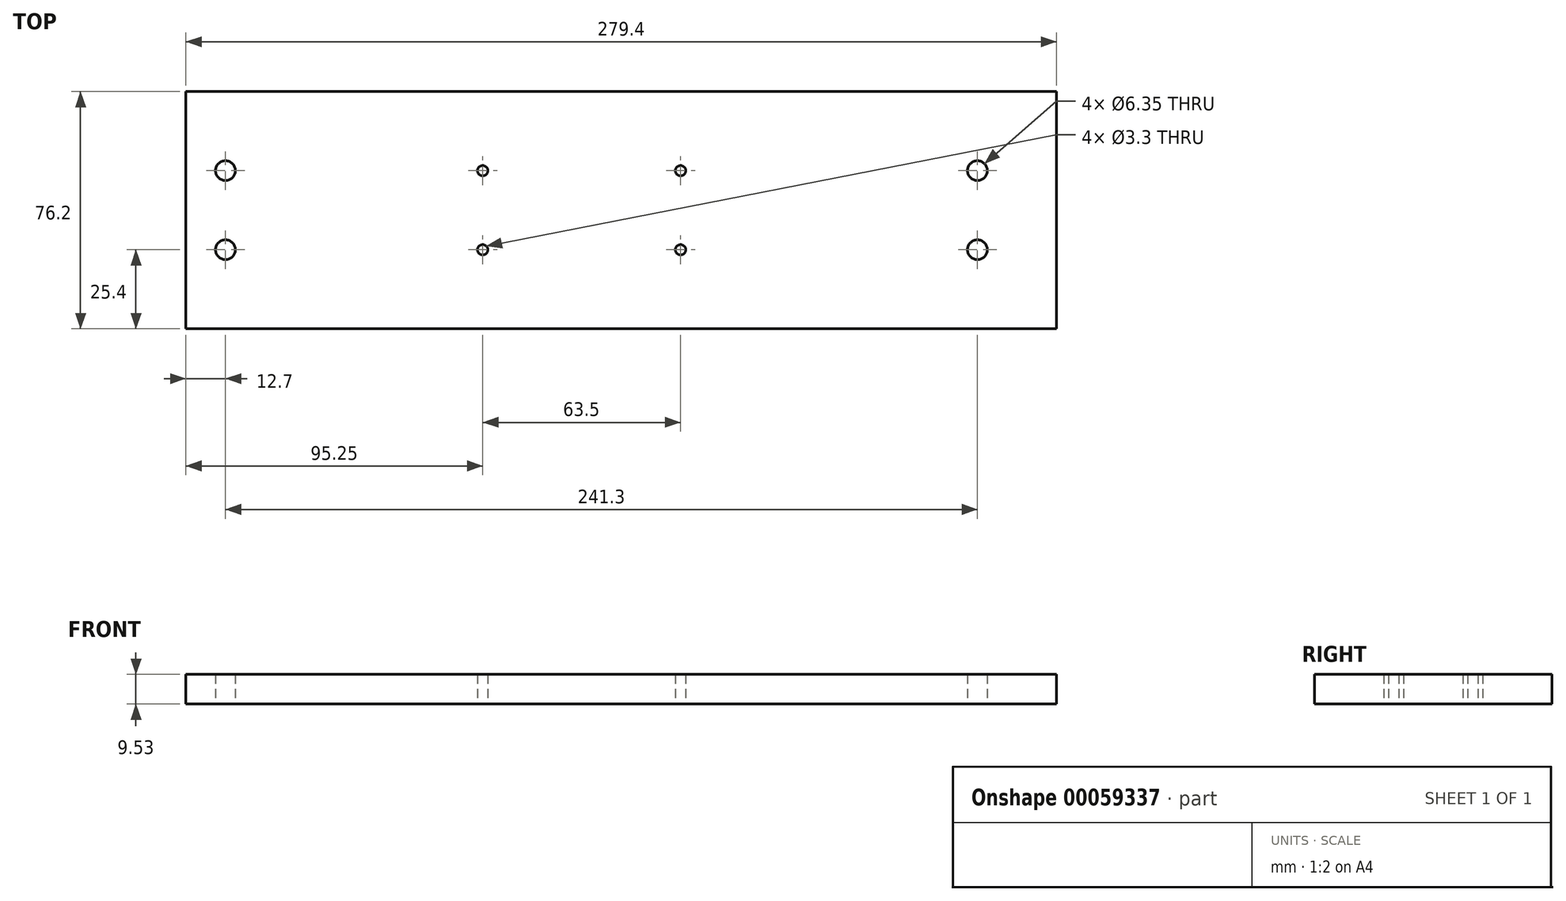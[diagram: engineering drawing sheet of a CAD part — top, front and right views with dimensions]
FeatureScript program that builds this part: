
annotation { "Feature Type Name" : "Feature", "Feature Type Description" : "" }
export const myFeature = defineFeature(function(context is Context, id is Id, definition is map)
    precondition{}
    {
        {
            var Q0;
            Q0=qCreatedBy(makeId("Top.planeOp"),FACE);
            var sketch = newSketch(context, id + "F0", { "sketchPlane" : qUnion([Q0])});
            skLineSegment(sketch, "E0.rect.bottom", {"start": v(139.7, -38.1) * mm, "end": v(-139.7, -38.1) * mm});
            skLineSegment(sketch, "E0.rect.top", {"start": v(139.7, 38.1) * mm, "end": v(-139.7, 38.1) * mm});
            skLineSegment(sketch, "E0.rect.left", {"start": v(139.7, -38.1) * mm, "end": v(139.7, 38.1) * mm});
            skLineSegment(sketch, "E0.rect.right", {"start": v(-139.7, -38.1) * mm, "end": v(-139.7, 38.1) * mm});
            skPoint(sketch, "E0.rect.middle", {"position": v(0, 0) * mm});
            skCircle(sketch, "E1", {"center": v(-127, 12.7) * mm, "radius": 3.18 * mm});
            skCircle(sketch, "E2", {"center": v(114.3, 12.7) * mm, "radius": 3.18 * mm});
            skCircle(sketch, "E3", {"center": v(-44.45, 12.7) * mm, "radius": 1.65 * mm});
            skCircle(sketch, "E4", {"center": v(19.05, 12.7) * mm, "radius": 1.65 * mm});
            skCircle(sketch, "E5.MirrorC", {"center": v(-127, -12.7) * mm, "radius": 3.18 * mm});
            skCircle(sketch, "E6.MirrorC", {"center": v(-44.45, -12.7) * mm, "radius": 1.65 * mm});
            skCircle(sketch, "E7.MirrorC", {"center": v(19.05, -12.7) * mm, "radius": 1.65 * mm});
            skCircle(sketch, "E8.MirrorC", {"center": v(114.3, -12.7) * mm, "radius": 3.18 * mm});
            skSolve(sketch);
        }
        {
            var Q0;
            Q0=makeQuery(id+"F0.imprint","IMPRINT",FACE,{"disambiguationData":[TD([[makeQuery(id+"F0.imprint","IMPRINT",EDGE,{"derivedFrom":sQuery(id+"F0.wireOp",EDGE,"E0.rect.bottom")}),-1.0]])]});
            extrude(context, id + "F1", {"entities" : qUnion([Q0]), "depth" : 9.52 * mm});
        }
    });
